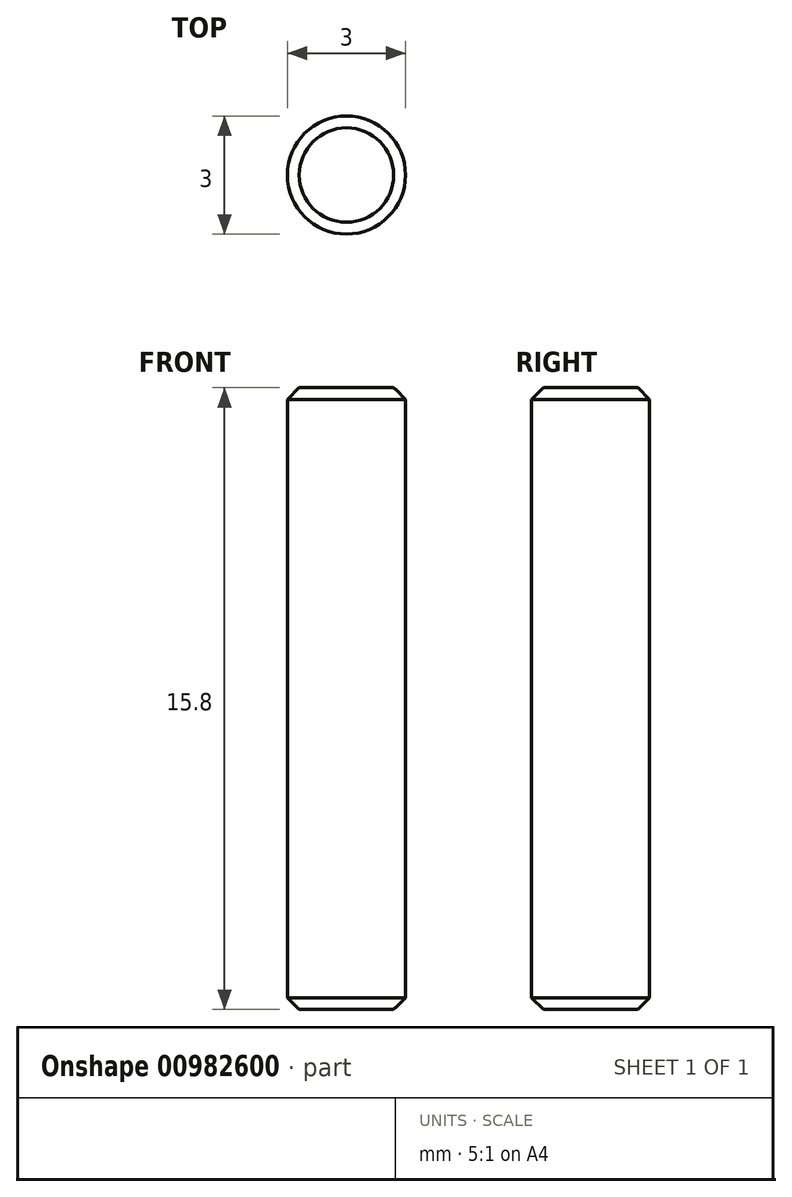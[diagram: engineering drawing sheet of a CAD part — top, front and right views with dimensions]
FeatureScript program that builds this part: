
annotation { "Feature Type Name" : "Feature", "Feature Type Description" : "" }
export const myFeature = defineFeature(function(context is Context, id is Id, definition is map)
    precondition{}
    {
        {
            var Q0;
            Q0=qCreatedBy(makeId("Top.planeOp"),FACE);
            var sketch = newSketch(context, id + "F0", { "sketchPlane" : qUnion([Q0])});
            skCircle(sketch, "E0", {"center": v(0, 0) * mm, "radius": 1.5 * mm});
            skSolve(sketch);
        }
        {
            var Q0;
            Q0=qSketchRegion(id+"F0",true);
            extrude(context, id + "F1", {"entities" : qUnion([Q0]), "depth" : 15.8 * mm});
        }
        {
            var Q0;
            Q0=makeQuery(id+"F1.opExtrude","CAP_EDGE",EDGE,{"disambiguationData":[OSD([sQuery(id+"F0.wireOp",EDGE,"E0")])],"isStart":false});
            var Q1;
            Q1=makeQuery(id+"F1.opExtrude","CAP_EDGE",EDGE,{"disambiguationData":[OSD([sQuery(id+"F0.wireOp",EDGE,"E0")])],"isStart":true});
            chamfer(context, id + "F2", {"entities" : qUnion([Q0, Q1]), "width" : .3 * mm, "tangentPropagation" : true});
        }
    });
